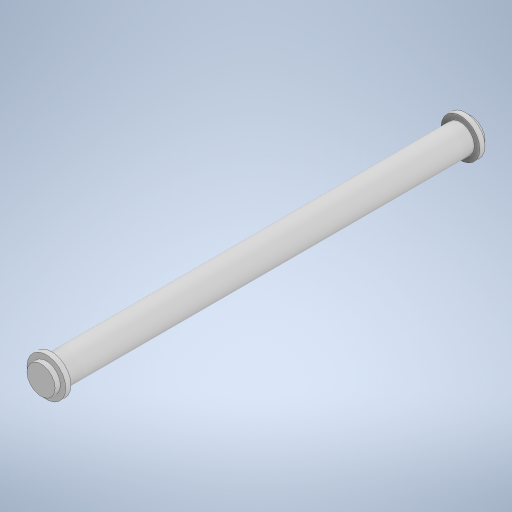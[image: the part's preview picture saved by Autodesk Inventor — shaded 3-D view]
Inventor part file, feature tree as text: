
AUTODESK INVENTOR PART (.ipt)
format: ipt  version: 2023 (Build 270158000, 158)  size: 256,000 bytes
history: native  units: in
note: dims shown in document units (in); Inventor stores cm internally (conversion verified against a paired STEP export)
features: extrude x5, sketch x5
ambient origin geometry x8: Origin, YZ Plane, XZ Plane, XY Plane, X Axis, Y Axis, Z Axis, Center Point
bodies: Solid1 (feature_tree)
feature tree (10):
  extrude  "Extrusion1"  Depth=116.0in TaperAngle=0.0deg
  extrude  "Extrusion2"  Depth=1.5in TaperAngle=0.0deg
  extrude  "Extrusion3"  Depth=1.5in TaperAngle=0.0deg
  extrude  "Extrusion4"  Depth=1.5in
  extrude  "Extrusion5"  Depth=0.5in
  sketch  "Sketch1"  dims[d0=8.0in d1=116.0in d2=0.0in]
  sketch  "Sketch2"  dims[d3=11.0in d4=1.5in d5=0.0in]
  sketch  "Sketch3"  dims[d6=1.5in d7=0.0in d8=1.5in d9=0.0in]
  sketch  "Sketch4"  dims[d10=1.5in d11=0.0in d12=0.5in]
  sketch  "Sketch5"  dims[d13=0.0344in d14=0.5in d15=0.0344in]
